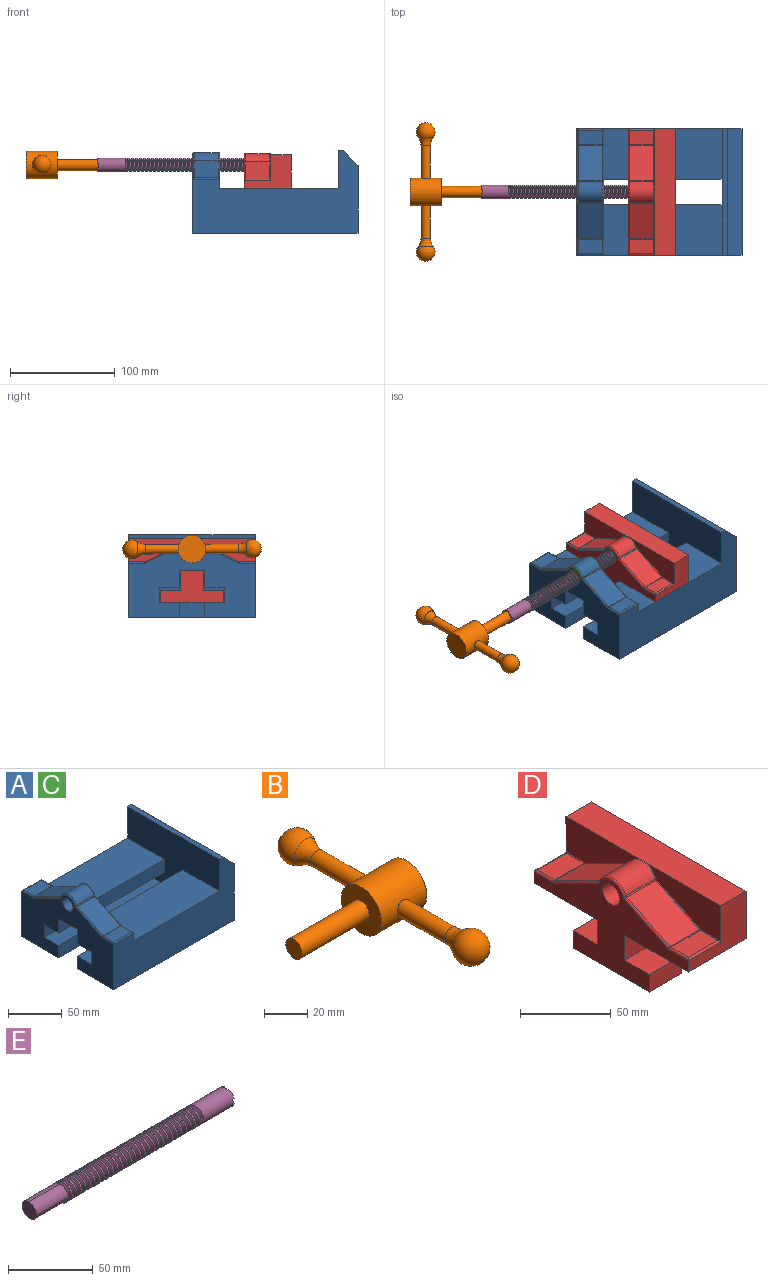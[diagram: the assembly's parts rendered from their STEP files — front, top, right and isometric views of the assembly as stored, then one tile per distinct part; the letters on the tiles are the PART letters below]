
ASSEMBLY  parts=5 mates=3
PART A: 52 faces, bbox 157.2x120.4x78.7 mm
  f0: plane 120.43x64.61mm, normal (1,0,0), area 7781.3mm2, adj f2,f7,f8,f51
  f1: plane 120.43x32.9mm, normal (1,0,0), area 1898.6mm2, adj f2,f7,f13,f14,f15,f21,f22,f26
  f2: plane 157.23x78.66mm, normal (0,1,0), area 7529.6mm2, adj f0,f1,f8,f20,f22,f23,f24,f29
  f3: plane 22.86x13.68mm, normal (0,0,1), area 312.7mm2, adj f27,f29,f33,f34
  f4: plane 34.13x22.86mm, normal (0,0.44,0.9), area 868mm2, adj f34,f35,f44,f45
  f5: plane 33.93x22.86mm, normal (0,-0.43,0.9), area 858.6mm2, adj f37,f38,f46,f47
  f6: plane 22.86x13.68mm, normal (0,0,1), area 312.8mm2, adj f28,f32,f38,f39
  f7: plane 157.23x78.66mm, normal (0,-1,0), area 7529.6mm2, adj f0,f1,f8,f20,f21,f23,f24,f32
  f8: plane 157.23x120.43mm, normal (0,0,-1), area 15631.9mm2, adj f0,f2,f7,f9,f19,f20,f24
  f9: plane 138.18x13.98mm, normal (0,1,0), area 1932.1mm2, adj f8,f10,f20,f24
  f10: plane 138.18x18.94mm, normal (0,0,1), area 2617.7mm2, adj f9,f11,f20,f24
  f11: plane 138.18x14.12mm, normal (0,1,0), area 1950.7mm2, adj f10,f12,f20,f24
  f12: plane 138.18x18.94mm, normal (0,0,-1), area 2617.7mm2, adj f11,f13,f20,f24
  f13: plane 138.18x16.1mm, normal (0,1,0), area 2061.6mm2, adj f1,f12,f14,f20,f21,f24
  f14: plane 25.4x23.91mm, normal (0,0,-1), area 607.2mm2, adj f1,f13,f15,f20
  f15: plane 138.18x16.1mm, normal (0,-1,0), area 2061.6mm2, adj f1,f14,f16,f20,f22,f24
  f16: plane 138.18x18.94mm, normal (0,0,-1), area 2617.7mm2, adj f15,f17,f20,f24
  f17: plane 138.18x14.12mm, normal (0,-1,0), area 1950.7mm2, adj f16,f18,f20,f24
  f18: plane 138.18x18.94mm, normal (0,0,1), area 2617.7mm2, adj f17,f19,f20,f24
  f19: plane 138.18x13.98mm, normal (0,-1,0), area 1932.1mm2, adj f8,f18,f20,f24
  f20: plane 120.43x75.65mm, normal (-1,0,0), area 5490.6mm2, adj f2,f7,f8,f9,f10,f11,f12,f13
  f21: plane 112.78x48.26mm, normal (0,0,1), area 5442.9mm2, adj f1,f7,f13,f24
  f22: plane 112.78x48.26mm, normal (0,0,1), area 5442.9mm2, adj f1,f2,f15,f24
  f23: plane 120.43x5mm, normal (0,0,1), area 602mm2, adj f2,f7,f24,f51
  f24: plane 120.43x78.66mm, normal (-1,0,0), area 5881.6mm2, adj f2,f7,f8,f9,f10,f11,f12,f13
  f25: cylinder r=10.74mm len=22.86mm, axis (-1,0,0), area 594.4mm2, adj f36,f45,f46,f50
  f26: cylinder r=6.6mm len=25.4mm, axis (-1,0,0), area 1054mm2, adj f1,f20
  f27: cylinder r=1.27mm len=14.95mm, axis (0,1,0), area 28.9mm2, adj f1,f3,f29,f30
  f28: cylinder r=1.27mm len=14.95mm, axis (0,1,0), area 28.9mm2, adj f1,f6,f31,f32
  f29: cylinder r=1.27mm len=25.4mm, axis (-1,0,0), area 48.8mm2, adj f2,f3,f27,f33
  f30: torus R=2.54mm, axis (1,0,0), area 1.6mm2, adj f1,f27,f34,f35
  f31: torus R=2.54mm, axis (1,0,0), area 1.5mm2, adj f1,f28,f37,f38
  f32: cylinder r=1.27mm len=25.4mm, axis (1,0,0), area 48.8mm2, adj f6,f7,f28,f39
  f33: cylinder r=1.27mm len=14.95mm, axis (0,-1,0), area 28.9mm2, adj f3,f20,f29,f40
  f34: cylinder r=1.27mm len=22.86mm, axis (-1,0,0), area 13.2mm2, adj f3,f4,f30,f40
  f35: cylinder r=1.27mm len=34.69mm, axis (0,0.9,-0.44), area 75.7mm2, adj f1,f4,f30,f41
  f36: torus R=9.47mm, axis (1,0,0), area 49.6mm2, adj f1,f25,f41,f42
  f37: cylinder r=1.27mm len=34.47mm, axis (0,0.9,0.43), area 74.9mm2, adj f1,f5,f31,f42
  f38: cylinder r=1.27mm len=22.86mm, axis (1,0,0), area 12.9mm2, adj f5,f6,f31,f43
  f39: cylinder r=1.27mm len=14.95mm, axis (0,-1,0), area 28.9mm2, adj f6,f20,f32,f43
  f40: torus R=2.54mm, axis (1,0,0), area 1.6mm2, adj f20,f33,f34,f44
  f41: torus R=2.54mm, axis (1,0,0), area 2.5mm2, adj f1,f35,f36,f45
  f42: torus R=2.54mm, axis (1,0,0), area 2.7mm2, adj f1,f36,f37,f46
  f43: torus R=2.54mm, axis (1,0,0), area 1.5mm2, adj f20,f38,f39,f47
  f44: cylinder r=1.27mm len=34.69mm, axis (0,-0.9,0.44), area 75.7mm2, adj f4,f20,f40,f48
  f45: cylinder r=1.27mm len=22.86mm, axis (-1,0,0), area 21.3mm2, adj f4,f25,f41,f48
  f46: cylinder r=1.27mm len=22.86mm, axis (-1,0,0), area 22.9mm2, adj f5,f25,f42,f49
  f47: cylinder r=1.27mm len=34.47mm, axis (0,-0.9,-0.43), area 74.9mm2, adj f5,f20,f43,f49
  f48: torus R=2.54mm, axis (1,0,0), area 2.5mm2, adj f20,f44,f45,f50
  f49: torus R=2.54mm, axis (1,0,0), area 2.7mm2, adj f20,f46,f47,f50
  f50: torus R=9.47mm, axis (1,0,0), area 49.6mm2, adj f20,f25,f48,f49
  f51: plane 120.43x14.05mm, normal (0.71,0,0.71), area 2393.2mm2, adj f0,f2,f7,f23
PART B: 15 faces, bbox 74.2x132.1x26.4 mm
  f0: cylinder r=4.45mm len=31.61mm, axis (0,1,0), area 872mm2, adj f2,f9
  f1: cylinder r=4.45mm len=31.61mm, axis (0,1,0), area 871.9mm2, adj f2,f10
  f2: cylinder r=13.19mm len=29.97mm, axis (-1,0,0), area 2357.9mm2, adj f0,f1,f5,f6
  f3: cylinder r=5.3mm len=44.2mm, axis (-1,0,0), area 1472.4mm2, adj f4,f6
  f4: plane 10.6x10.6mm, normal (-1,0,0), area 88.3mm2, adj f3
  f5: plane 26.38x26.38mm, normal (1,0,0), area 546.6mm2, adj f2
  f6: plane 26.38x26.38mm, normal (-1,0,0), area 458.3mm2, adj f2,f3
  f7: sphere r=8.89mm, area 798.4mm2, adj f10
  f8: sphere r=8.89mm, area 798.4mm2, adj f9
  f9: torus R=17.14mm, axis (0,1,0), area 277.8mm2, adj f0,f8
  f10: torus R=17.14mm, axis (0,-1,0), area 277.8mm2, adj f1,f7
  f11: sphere r=4.45mm, area 124.1mm2, adj f12
  f12: plane 8.89x8.89mm, normal (0,-1,0), area 62.1mm2, adj f11
  f13: sphere r=4.45mm, area 124.1mm2, adj f14
  f14: plane 8.89x8.89mm, normal (0,1,0), area 62.1mm2, adj f13
PART C: same geometry as A
PART D: 48 faces, bbox 45x120.6x62.5 mm
  f0: plane 25.15x7.54mm, normal (0,1,0), area 189.7mm2, adj f12,f19,f28,f43
  f1: cylinder r=6.6mm len=25.15mm, axis (-1,0,0), area 1043.4mm2, adj f28,f47
  f2: cylinder r=1.27mm len=25.15mm, axis (1,0,0), area 48.7mm2, adj f3,f17,f18,f30,f46
  f3: cylinder r=1.27mm len=14.7mm, axis (0,1,0), area 16.8mm2, adj f2,f4,f17,f46
  f4: torus R=2.54mm, axis (1,0,0), area 0.8mm2, adj f3,f5,f29,f46
  f5: cylinder r=1.27mm len=34.15mm, axis (0,0.9,0.43), area 44.2mm2, adj f4,f6,f16,f46
  f6: torus R=2.54mm, axis (1,0,0), area 1.3mm2, adj f5,f7,f32,f46
  f7: torus R=9.47mm, axis (1,0,0), area 31mm2, adj f6,f8,f15,f43,f44,f46
  f8: torus R=2.54mm, axis (1,0,0), area 1.2mm2, adj f7,f9,f35,f43
  f9: cylinder r=1.27mm len=34.35mm, axis (0,0.9,-0.44), area 44.7mm2, adj f8,f10,f14,f43
  f10: torus R=2.54mm, axis (1,0,0), area 0.8mm2, adj f9,f11,f38,f43
  f11: cylinder r=1.27mm len=14.69mm, axis (0,1,0), area 16.8mm2, adj f10,f12,f13,f43
  f12: cylinder r=1.27mm len=25.15mm, axis (-1,0,0), area 48.7mm2, adj f0,f11,f13,f41,f43
  f13: plane 22.86x13.68mm, normal (0,0,1), area 312.7mm2, adj f11,f12,f38,f41
  f14: plane 34.13x22.86mm, normal (0,0.44,0.9), area 868mm2, adj f9,f35,f38,f39
  f15: cylinder r=10.74mm len=22.86mm, axis (-1,0,0), area 594mm2, adj f7,f32,f35,f36
  f16: plane 33.93x22.86mm, normal (0,-0.43,0.9), area 858.6mm2, adj f5,f29,f32,f33
  f17: plane 22.86x13.68mm, normal (0,0,1), area 312.8mm2, adj f2,f3,f29,f30
  f18: plane 44.96x32.2mm, normal (0,-1,0), area 827.6mm2, adj f2,f19,f28,f42,f44,f46
  f19: plane 120.5x44.96mm, normal (0,0,-1), area 4880.3mm2, adj f0,f18,f20,f26,f27,f28,f42,f43
  f20: plane 25.4x16.89mm, normal (0,-1,0), area 428.9mm2, adj f19,f21,f27,f28
  f21: plane 25.4x19.22mm, normal (0,0,1), area 488.1mm2, adj f20,f22,f27,f28
  f22: plane 25.4x11.79mm, normal (0,-1,0), area 299.5mm2, adj f21,f23,f27,f28
  f23: plane 59.5x25.4mm, normal (0,0,-1), area 1511.4mm2, adj f22,f24,f27,f28
  f24: plane 25.4x11.79mm, normal (0,1,0), area 299.5mm2, adj f23,f25,f27,f28
  f25: plane 25.4x19.22mm, normal (0,0,1), area 488.1mm2, adj f24,f26,f27,f28
  f26: plane 25.4x16.89mm, normal (0,1,0), area 428.9mm2, adj f19,f25,f27,f28
  f27: plane 59.5x28.68mm, normal (1,0,0), area 1057.5mm2, adj f19,f20,f21,f22,f23,f24,f25,f26
  f28: plane 120.43x60.36mm, normal (-1,0,0), area 2845mm2, adj f0,f1,f18,f19,f20,f21,f22,f23
  f29: cylinder r=1.27mm len=22.86mm, axis (1,0,0), area 12.9mm2, adj f4,f16,f17,f31
  f30: cylinder r=1.27mm len=14.95mm, axis (0,-1,0), area 28.9mm2, adj f2,f17,f28,f31
  f31: torus R=2.54mm, axis (1,0,0), area 1.5mm2, adj f28,f29,f30,f33
  f32: cylinder r=1.27mm len=22.86mm, axis (-1,0,0), area 22.9mm2, adj f6,f15,f16,f34
  f33: cylinder r=1.27mm len=34.47mm, axis (0,-0.9,-0.43), area 74.9mm2, adj f16,f28,f31,f34
  f34: torus R=2.54mm, axis (1,0,0), area 2.7mm2, adj f28,f32,f33,f36
  f35: cylinder r=1.27mm len=22.86mm, axis (-1,0,0), area 21.3mm2, adj f8,f14,f15,f37
  f36: torus R=9.47mm, axis (1,0,0), area 49.6mm2, adj f15,f28,f34,f37
  f37: torus R=2.54mm, axis (1,0,0), area 2.5mm2, adj f28,f35,f36,f39
  f38: cylinder r=1.27mm len=22.86mm, axis (-1,0,0), area 13.2mm2, adj f10,f13,f14,f40
  f39: cylinder r=1.27mm len=34.69mm, axis (0,-0.9,0.44), area 75.7mm2, adj f14,f28,f37,f40
  f40: torus R=2.54mm, axis (1,0,0), area 1.6mm2, adj f28,f38,f39,f41
  f41: cylinder r=1.27mm len=14.95mm, axis (0,-1,0), area 28.9mm2, adj f12,f13,f28,f40
  f42: plane 120.63x32.2mm, normal (1,0,0), area 3882.1mm2, adj f18,f19,f44,f45
  f43: plane 58.18x32.2mm, normal (-1,0,0), area 926.4mm2, adj f0,f7,f8,f9,f10,f11,f12,f19
  f44: plane 120.63x19.81mm, normal (0,0,1), area 2389.4mm2, adj f7,f18,f42,f43,f45,f46
  f45: plane 32.2x19.81mm, normal (0,1,0), area 637.9mm2, adj f19,f42,f43,f44
  f46: plane 57.98x24.66mm, normal (-1,0,0), area 929.5mm2, adj f2,f3,f4,f5,f6,f7,f18,f44
  f47: plane 13.21x13.21mm, normal (-1,0,0), area 137mm2, adj f1
PART E: 55 faces, bbox 165.1x13.2x15.2 mm
  f0: plane 4.39x4.39mm, normal (1,0,0), area 6.9mm2, adj f2,f35,f43,f50
  f1: plane 4.39x4.39mm, normal (1,0,0), area 6.9mm2, adj f2,f35,f44,f53
  f2: cylinder r=6.58mm len=30.16mm, axis (-1,0,0), area 1126.1mm2, adj f0,f1,f32,f33,f34,f36,f37,f38
  f3: cylinder r=6.58mm len=13.16mm, axis (-1,0,0), area 52.5mm2, adj f4,f31,f36,f37
  f4: cylinder r=6.58mm len=13.16mm, axis (-1,0,0), area 52.5mm2, adj f3,f5,f36,f37
  f5: cylinder r=6.58mm len=13.16mm, axis (-1,0,0), area 52.5mm2, adj f4,f6,f36,f37
  f6: cylinder r=6.58mm len=13.16mm, axis (-1,0,0), area 52.5mm2, adj f5,f7,f36,f37
  f7: cylinder r=6.58mm len=13.16mm, axis (-1,0,0), area 52.5mm2, adj f6,f8,f36,f37
  f8: cylinder r=6.58mm len=13.16mm, axis (-1,0,0), area 52.5mm2, adj f7,f9,f36,f37
  f9: cylinder r=6.58mm len=13.16mm, axis (-1,0,0), area 52.5mm2, adj f8,f10,f36,f37
  f10: cylinder r=6.58mm len=13.16mm, axis (-1,0,0), area 52.5mm2, adj f9,f11,f36,f37
  f11: cylinder r=6.58mm len=13.16mm, axis (-1,0,0), area 52.5mm2, adj f10,f12,f36,f37
  f12: cylinder r=6.58mm len=13.16mm, axis (-1,0,0), area 52.5mm2, adj f11,f13,f36,f37
  f13: cylinder r=6.58mm len=13.16mm, axis (-1,0,0), area 52.5mm2, adj f12,f14,f36,f37
  f14: cylinder r=6.58mm len=13.16mm, axis (-1,0,0), area 52.5mm2, adj f13,f15,f36,f37
  f15: cylinder r=6.58mm len=13.16mm, axis (-1,0,0), area 52.5mm2, adj f14,f16,f36,f37
  f16: cylinder r=6.58mm len=13.16mm, axis (-1,0,0), area 52.5mm2, adj f15,f17,f36,f37
  f17: cylinder r=6.58mm len=13.16mm, axis (-1,0,0), area 52.5mm2, adj f16,f18,f36,f37
  f18: cylinder r=6.58mm len=13.16mm, axis (-1,0,0), area 52.5mm2, adj f17,f19,f36,f37
  f19: cylinder r=6.58mm len=13.16mm, axis (-1,0,0), area 52.5mm2, adj f18,f20,f36,f37
  f20: cylinder r=6.58mm len=13.16mm, axis (-1,0,0), area 52.5mm2, adj f19,f21,f36,f37
  f21: cylinder r=6.58mm len=13.16mm, axis (-1,0,0), area 52.5mm2, adj f20,f22,f36,f37
  f22: cylinder r=6.58mm len=13.16mm, axis (-1,0,0), area 52.5mm2, adj f21,f23,f36,f37
  f23: cylinder r=6.58mm len=13.16mm, axis (-1,0,0), area 52.5mm2, adj f22,f24,f36,f37
  f24: cylinder r=6.58mm len=13.16mm, axis (-1,0,0), area 52.5mm2, adj f23,f25,f36,f37
  f25: cylinder r=6.58mm len=13.16mm, axis (-1,0,0), area 52.5mm2, adj f24,f26,f36,f37
  f26: cylinder r=6.58mm len=13.16mm, axis (-1,0,0), area 52.5mm2, adj f25,f27,f36,f37
  f27: cylinder r=6.58mm len=13.16mm, axis (-1,0,0), area 52.5mm2, adj f26,f28,f36,f37
  f28: cylinder r=6.58mm len=13.16mm, axis (-1,0,0), area 52.5mm2, adj f27,f29,f36,f37
  f29: cylinder r=6.58mm len=29.53mm, axis (-1,0,0), area 310.1mm2, adj f28,f30,f36,f37,f40,f41
  f30: cylinder r=6.58mm len=25.72mm, axis (-1,0,0), area 88mm2, adj f29,f37,f39,f41
  f31: cylinder r=6.58mm len=13.16mm, axis (-1,0,0), area 52.5mm2, adj f3,f32,f36,f37
  f32: cylinder r=6.58mm len=13.16mm, axis (-1,0,0), area 52.5mm2, adj f2,f31,f36,f37
  f33: plane 4.39x4.39mm, normal (1,0,0), area 6.9mm2, adj f2,f35,f46,f49
  f34: plane 4.39x4.39mm, normal (1,0,0), area 6.9mm2, adj f2,f35,f47,f52
  f35: cylinder r=5.31mm len=10.63mm, axis (1,0,0), area 196.2mm2, adj f0,f1,f33,f34,f42,f43,f44,f45
  f36: bspline ~115.57x15.19mm, area 2622mm2, adj f2,f3,f4,f5,f6,f7,f8,f9
  f37: bspline ~114.3x15.19mm, area 2587.1mm2, adj f2,f3,f4,f5,f6,f7,f8,f9
  f38: plane 2.54x2.2mm, normal (0,0,1), area 2.8mm2, adj f2,f36,f37
  f39: bspline ~25.4x9.49mm, area 296.8mm2, adj f30,f37,f40,f41
  f40: bspline ~25.4x8.77mm, area 296.8mm2, adj f29,f36,f39,f41
  f41: plane 12.17x11.64mm, normal (-1,0,0), area 109.1mm2, adj f29,f30,f39,f40
  f42: plane 10.63x10.63mm, normal (1,0,0), area 88.7mm2, adj f35
  f43: plane 1.34x1.02mm, normal (0,1,0), area 1.4mm2, adj f0,f2,f35,f45
  f44: plane 1.34x1.02mm, normal (0,-1,0), area 1.4mm2, adj f1,f2,f35,f45
  f45: plane 3.81x1.62mm, normal (1,0,0), area 4.9mm2, adj f2,f35,f43,f44
  f46: plane 1.34x1.02mm, normal (0,1,0), area 1.4mm2, adj f2,f33,f35,f48
  f47: plane 1.34x1.02mm, normal (0,-1,0), area 1.4mm2, adj f2,f34,f35,f48
  f48: plane 3.81x1.62mm, normal (1,0,0), area 4.9mm2, adj f2,f35,f46,f47
  f49: plane 1.34x1.02mm, normal (0,0,1), area 1.4mm2, adj f2,f33,f35,f51
  f50: plane 1.34x1.02mm, normal (0,0,-1), area 1.4mm2, adj f0,f2,f35,f51
  f51: plane 3.81x1.62mm, normal (1,0,0), area 4.9mm2, adj f2,f35,f49,f50
  f52: plane 1.34x1.02mm, normal (0,0,1), area 1.4mm2, adj f2,f34,f35,f54
  f53: plane 1.34x1.02mm, normal (0,0,-1), area 1.4mm2, adj f1,f2,f35,f54
  f54: plane 3.81x1.62mm, normal (1,0,0), area 4.9mm2, adj f2,f35,f52,f53
PLACE A t=(-123.71,-1.51,23.85)mm fixed
PLACE B rot(axis=(0,0,-1),180deg) t=(-208.55,-1.57,62.43)mm
PLACE C t=(-123.71,-1.51,23.85)mm
PLACE D t=(-74.95,-1.57,29.52)mm
PLACE E rot(axis=(0,0,-1),180deg) t=(-132.35,-1.57,62.43)mm
MATE slider A.f24 <-> D.f42  axis (1,0,0) through (14.47,58.71,40.22)mm
MATE revolute D.f1 <-> E.f2  axis (-1,0,0) through (-49.8,-1.57,62.43)mm
MATE fastened E.f35 <-> B.f3  axis (-1,0,0) through (-208.55,-1.57,62.43)mm
